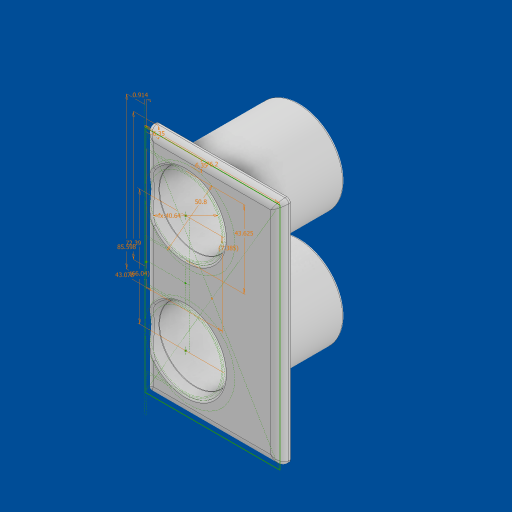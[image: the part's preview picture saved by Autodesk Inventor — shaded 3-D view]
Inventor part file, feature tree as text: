
AUTODESK INVENTOR PART (.ipt)
format: ipt  version: 2023.2 (Build 272271000, 271)  size: 290,816 bytes
history: native  units: mm
features: fillet x3, chamfer x3, sketch x2, extrude x2, hole x1
ambient origin geometry x8: Origin, YZ Plane, XZ Plane, XY Plane, X Axis, Y Axis, Z Axis, Center Point
bodies: Solid1 (feature_tree)
feature tree (11):
  sketch  "Sketch1"  dims[d0=76.2mm d2=50.8mm]
  extrude  "Extrusion1"  Depth=50.8mm
  extrude  "Extrusion2"  Depth=1.0mm
  hole  "Hole1"  [1 undecoded]
  fillet  "Fillet1"  Radius=85.598mm
  chamfer  "Chamfer1"  Distance=6.35mm
  chamfer  "Chamfer2"  Distance=72.39mm
  chamfer  "Chamfer3"  Distance=20.0mm
  fillet  "Fillet2"  Radius=6.0mm
  fillet  "Fillet3"  Radius=55.88mm
  sketch  "Sketch2"  dims[d3=43.0784mm d4=0.9144mm d5=43.6245mm d6=85.598mm d7=6.35mm d8=72.39mm d9=20.0mm d11=66.04mm d12=10.0mm d14=10.0mm d16=6.0mm d17=0.0mm d18=55.88mm d19=0.0mm d20=6.35mm d21=40.64mm d22=6.0mm d23=4.4mm d24=2.0mm d25=90.0deg d26=8.0mm d27=0.0mm d28=40.64mm d29=7.38505mm d30=2.0mm d31=2.0mm d32=2.0mm d33=12.217305mm d34=2.0mm d35=2.0mm d36=12.217305mm d37=2.0mm d38=2.0mm d39=12.217305mm d40=5.0mm d41=1.0mm]
note: 1 required parameter value undecoded (feature->parameter linkage not recoverable at this tier; creation-order binding heuristic only, values carry confidence <= 0.55)
